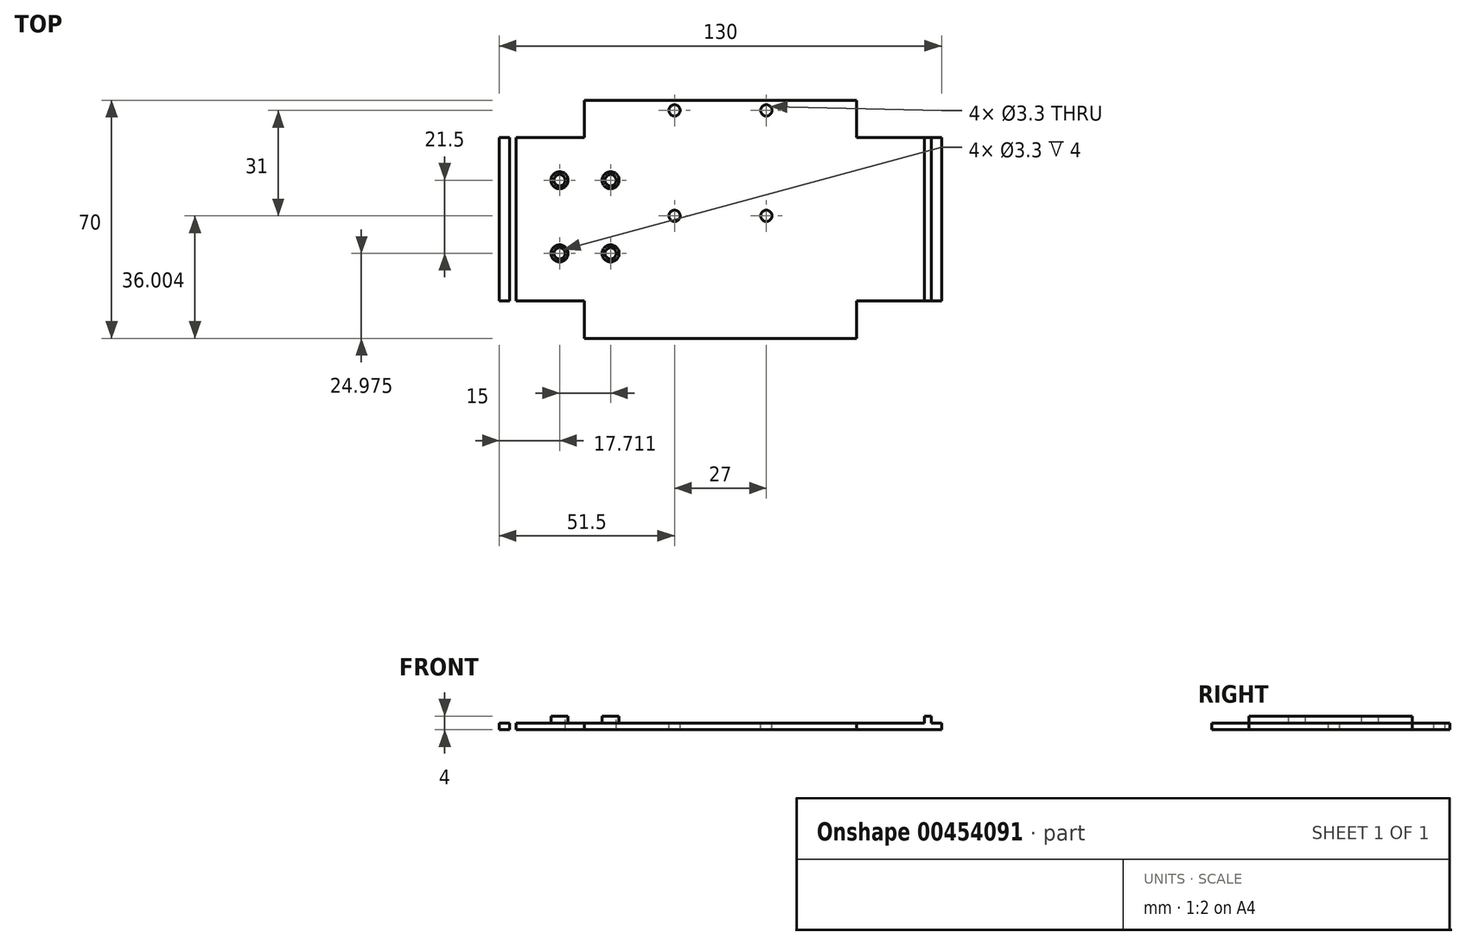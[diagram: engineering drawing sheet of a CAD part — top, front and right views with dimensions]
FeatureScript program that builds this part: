
annotation { "Feature Type Name" : "Feature", "Feature Type Description" : "" }
export const myFeature = defineFeature(function(context is Context, id is Id, definition is map)
    precondition{}
    {
        {
            var Q0;
            Q0=qCreatedBy(makeId("Top.planeOp"),FACE);
            var sketch = newSketch(context, id + "F0", { "sketchPlane" : qUnion([Q0])});
            skLineSegment(sketch, "E0.bottom", {"start": v(-50.01, 37.07) * mm, "end": v(29.99, 37.07) * mm});
            skLineSegment(sketch, "E0.top", {"start": v(-50.01, -32.93) * mm, "end": v(29.99, -32.93) * mm});
            skLineSegment(sketch, "E0.left", {"start": v(-50.01, 37.07) * mm, "end": v(-50.01, -32.93) * mm});
            skLineSegment(sketch, "E0.right", {"start": v(29.99, 37.07) * mm, "end": v(29.99, -32.93) * mm});
            skLineSegment(sketch, "E1.bottom", {"start": v(-75.01, 26.07) * mm, "end": v(54.99, 26.07) * mm});
            skLineSegment(sketch, "E1.top", {"start": v(-75.01, -21.93) * mm, "end": v(54.99, -21.93) * mm});
            skLineSegment(sketch, "E1.left", {"start": v(-75.01, 26.07) * mm, "end": v(-75.01, -21.93) * mm});
            skLineSegment(sketch, "E1.right", {"start": v(54.99, 26.07) * mm, "end": v(54.99, -21.93) * mm});
            skLineSegment(sketch, "E2.bottom", {"start": v(-72.01, 26.07) * mm, "end": v(-70.01, 26.07) * mm});
            skLineSegment(sketch, "E2.top", {"start": v(-72.01, -21.93) * mm, "end": v(-70.01, -21.93) * mm});
            skLineSegment(sketch, "E2.left", {"start": v(-72.01, 26.07) * mm, "end": v(-72.01, -21.93) * mm});
            skLineSegment(sketch, "E2.right", {"start": v(-70.01, 26.07) * mm, "end": v(-70.01, -21.93) * mm});
            skLineSegment(sketch, "E3.bottom", {"start": v(49.99, 26.07) * mm, "end": v(51.99, 26.07) * mm});
            skLineSegment(sketch, "E3.top", {"start": v(49.99, -21.93) * mm, "end": v(51.99, -21.93) * mm});
            skLineSegment(sketch, "E3.left", {"start": v(49.99, 26.07) * mm, "end": v(49.99, -21.93) * mm});
            skLineSegment(sketch, "E3.right", {"start": v(51.99, 26.07) * mm, "end": v(51.99, -21.93) * mm});
            skLineSegment(sketch, "E4.bottom", {"start": v(-23.51, 34.07) * mm, "end": v(3.49, 34.07) * mm, "construction": true});
            skLineSegment(sketch, "E4.top", {"start": v(-23.51, 3.07) * mm, "end": v(3.49, 3.07) * mm, "construction": true});
            skLineSegment(sketch, "E4.left", {"start": v(-23.51, 34.07) * mm, "end": v(-23.51, 3.07) * mm, "construction": true});
            skLineSegment(sketch, "E4.right", {"start": v(3.49, 34.07) * mm, "end": v(3.49, 3.07) * mm, "construction": true});
            skLineSegment(sketch, "E5.bottom", {"start": v(-54.29, 26.07) * mm, "end": v(-17.79, 26.07) * mm});
            skLineSegment(sketch, "E5.top", {"start": v(-54.29, -21.93) * mm, "end": v(-17.79, -21.93) * mm});
            skLineSegment(sketch, "E6.bottom", {"start": v(19.21, 26.07) * mm, "end": v(55.71, 26.07) * mm});
            skLineSegment(sketch, "E6.top", {"start": v(19.21, -21.93) * mm, "end": v(55.71, -21.93) * mm});
            skLineSegment(sketch, "E7.bottom", {"start": v(-57.3, 13.54) * mm, "end": v(-42.3, 13.54) * mm, "construction": true});
            skLineSegment(sketch, "E7.top", {"start": v(-57.3, -7.96) * mm, "end": v(-42.3, -7.96) * mm, "construction": true});
            skLineSegment(sketch, "E7.left", {"start": v(-57.3, 13.54) * mm, "end": v(-57.3, -7.96) * mm, "construction": true});
            skLineSegment(sketch, "E7.right", {"start": v(-42.3, 13.54) * mm, "end": v(-42.3, -7.96) * mm, "construction": true});
            skCircle(sketch, "E8", {"center": v(-57.3, 13.54) * mm, "radius": 2.5 * mm});
            skCircle(sketch, "E9", {"center": v(-42.3, 13.54) * mm, "radius": 2.5 * mm});
            skCircle(sketch, "E10", {"center": v(-42.3, -7.96) * mm, "radius": 2.5 * mm});
            skCircle(sketch, "E11", {"center": v(-57.3, -7.96) * mm, "radius": 2.5 * mm});
            skSolve(sketch);
        }
        {
            var Q0;
            {var subQ0=sQuery(id+"F0.wireOp",EDGE,"E1.bottom");var subQ1=sQuery(id+"F0.wireOp",EDGE,"E0.left");var subQ2=makeQuery(id+"F0.imprint","INTERSECT",VERTEX,{"derivedFrom":[subQ1,subQ0]});Q0=makeQuery(id+"F0.imprint","IMPRINT",FACE,{"disambiguationData":[TD([[makeQuery(id+"F0.imprint","IMPRINT",EDGE,{"disambiguationData":[TD([[subQ2,-1.0]])],"derivedFrom":subQ1}),1.0]])]});}
            var Q1;
            {var subQ0=sQuery(id+"F0.wireOp",EDGE,"E0.bottom");Q1=makeQuery(id+"F0.imprint","IMPRINT",FACE,{"disambiguationData":[TD([[makeQuery(id+"F0.imprint","IMPRINT",EDGE,{"derivedFrom":subQ0}),-1.0]])]});}
            var Q2;
            {var subQ5=sQuery(id+"F0.wireOp",EDGE,"E1.left");Q2=makeQuery(id+"F0.imprint","IMPRINT",FACE,{"disambiguationData":[TD([[makeQuery(id+"F0.imprint","IMPRINT",EDGE,{"derivedFrom":subQ5}),1.0]])]});}
            var Q3;
            {var subQ0=sQuery(id+"F0.wireOp",EDGE,"E0.top");Q3=makeQuery(id+"F0.imprint","IMPRINT",FACE,{"disambiguationData":[TD([[makeQuery(id+"F0.imprint","IMPRINT",EDGE,{"derivedFrom":subQ0}),1.0]])]});}
            var Q4;
            {var subQ5=sQuery(id+"F0.wireOp",EDGE,"E1.right");Q4=makeQuery(id+"F0.imprint","IMPRINT",FACE,{"disambiguationData":[TD([[makeQuery(id+"F0.imprint","IMPRINT",EDGE,{"derivedFrom":subQ5}),-1.0]])]});}
            var Q5;
            {var subQ5=sQuery(id+"F0.wireOp",EDGE,"E2.right");Q5=makeQuery(id+"F0.imprint","IMPRINT",FACE,{"disambiguationData":[TD([[makeQuery(id+"F0.imprint","IMPRINT",EDGE,{"derivedFrom":subQ5}),1.0]])]});}
            var Q6;
            Q6=makeQuery(id+"F0.imprint","IMPRINT",FACE,{"disambiguationData":[TD([[makeQuery(id+"F0.imprint","IMPRINT",EDGE,{"derivedFrom":sQuery(id+"F0.wireOp",EDGE,"E2.bottom")}),-1.0]])]});
            var Q7;
            {var subQ5=sQuery(id+"F0.wireOp",EDGE,"E3.left");Q7=makeQuery(id+"F0.imprint","IMPRINT",FACE,{"disambiguationData":[TD([[makeQuery(id+"F0.imprint","IMPRINT",EDGE,{"derivedFrom":subQ5}),-1.0]])]});}
            var Q8;
            Q8=makeQuery(id+"F0.imprint","IMPRINT",FACE,{"disambiguationData":[TD([[makeQuery(id+"F0.imprint","IMPRINT",EDGE,{"derivedFrom":sQuery(id+"F0.wireOp",EDGE,"E3.bottom")}),-1.0]])]});
            var Q9;
            {var subQ0=sQuery(id+"F0.wireOp",EDGE,"E5.right");Q9=makeQuery(id+"F0.imprint","IMPRINT",FACE,{"disambiguationData":[TD([[makeQuery(id+"F0.imprint","IMPRINT",EDGE,{"derivedFrom":subQ0}),1.0]])]});}
            var Q10;
            {var subQ5=sQuery(id+"F0.wireOp",EDGE,"E6.right");Q10=makeQuery(id+"F0.imprint","IMPRINT",FACE,{"disambiguationData":[TD([[makeQuery(id+"F0.imprint","IMPRINT",EDGE,{"derivedFrom":subQ5}),1.0]])]});}
            var Q11;
            Q11=makeQuery(id+"F0.imprint","IMPRINT",FACE,{"disambiguationData":[TD([[makeQuery(id+"F0.imprint","IMPRINT",EDGE,{"derivedFrom":sQuery(id+"F0.wireOp",EDGE,"E9")}),1.0]])]});
            var Q12;
            Q12=makeQuery(id+"F0.imprint","IMPRINT",FACE,{"disambiguationData":[TD([[makeQuery(id+"F0.imprint","IMPRINT",EDGE,{"derivedFrom":sQuery(id+"F0.wireOp",EDGE,"E10")}),1.0]])]});
            var Q13;
            Q13=makeQuery(id+"F0.imprint","IMPRINT",FACE,{"disambiguationData":[TD([[makeQuery(id+"F0.imprint","IMPRINT",EDGE,{"derivedFrom":sQuery(id+"F0.wireOp",EDGE,"E11")}),1.0]])]});
            var Q14;
            Q14=makeQuery(id+"F0.imprint","IMPRINT",FACE,{"disambiguationData":[TD([[makeQuery(id+"F0.imprint","IMPRINT",EDGE,{"derivedFrom":sQuery(id+"F0.wireOp",EDGE,"E8")}),1.0]])]});
            var Q15;
            Q15=makeQuery(id+"F0.imprint","IMPRINT",FACE,{"disambiguationData":[TD([[makeQuery(id+"F0.imprint","IMPRINT",EDGE,{"derivedFrom":sQuery(id+"F0.wireOp",EDGE,"E9")}),-1.0]])]});
            var Q16;
            {var subQ0=sQuery(id+"F0.wireOp",EDGE,"E3.left");Q16=makeQuery(id+"F0.imprint","IMPRINT",FACE,{"disambiguationData":[TD([[makeQuery(id+"F0.imprint","IMPRINT",EDGE,{"derivedFrom":subQ0}),1.0]])]});}
            extrude(context, id + "F1", {"entities" : qUnion([Q0, Q1, Q2, Q3, Q4, Q5, Q6, Q7, Q8, Q9, Q10, Q11, Q12, Q13, Q14, Q15, Q16]), "oppositeDirection" : true, "depth" : 2 * mm});
        }
        {
            var Q0;
            Q0=makeQuery(id+"F0.imprint","IMPRINT",FACE,{"disambiguationData":[TD([[makeQuery(id+"F0.imprint","IMPRINT",EDGE,{"derivedFrom":sQuery(id+"F0.wireOp",EDGE,"E2.bottom")}),-1.0]])]});
            var Q1;
            Q1=makeQuery(id+"F0.imprint","IMPRINT",FACE,{"disambiguationData":[TD([[makeQuery(id+"F0.imprint","IMPRINT",EDGE,{"derivedFrom":sQuery(id+"F0.wireOp",EDGE,"E3.bottom")}),-1.0]])]});
            var Q2;
            Q2=makeQuery(id+"F0.imprint","IMPRINT",FACE,{"disambiguationData":[TD([[makeQuery(id+"F0.imprint","IMPRINT",EDGE,{"derivedFrom":sQuery(id+"F0.wireOp",EDGE,"E8")}),1.0]])]});
            var Q3;
            Q3=makeQuery(id+"F0.imprint","IMPRINT",FACE,{"disambiguationData":[TD([[makeQuery(id+"F0.imprint","IMPRINT",EDGE,{"derivedFrom":sQuery(id+"F0.wireOp",EDGE,"E9")}),1.0]])]});
            var Q4;
            Q4=makeQuery(id+"F0.imprint","IMPRINT",FACE,{"disambiguationData":[TD([[makeQuery(id+"F0.imprint","IMPRINT",EDGE,{"derivedFrom":sQuery(id+"F0.wireOp",EDGE,"E10")}),1.0]])]});
            var Q5;
            Q5=makeQuery(id+"F0.imprint","IMPRINT",FACE,{"disambiguationData":[TD([[makeQuery(id+"F0.imprint","IMPRINT",EDGE,{"derivedFrom":sQuery(id+"F0.wireOp",EDGE,"E11")}),1.0]])]});
            var Q6;
            {var subQ0=sQuery(id+"F0.wireOp",EDGE,"E3.left");Q6=makeQuery(id+"F0.imprint","IMPRINT",FACE,{"disambiguationData":[TD([[makeQuery(id+"F0.imprint","IMPRINT",EDGE,{"derivedFrom":subQ0}),1.0]])]});}
            extrude(context, id + "F2", {"entities" : qUnion([Q0, Q1, Q2, Q3, Q4, Q5, Q6]), "operationType" : NewBodyOperationType.ADD, "depth" : 2 * mm});
        }
        {
            var Q0;
            Q0=sQuery(id+"F0.wireOp",VERTEX,"E4.top.start");
            var Q1;
            Q1=sQuery(id+"F0.wireOp",VERTEX,"E4.right.end");
            var Q2;
            Q2=sQuery(id+"F0.wireOp",VERTEX,"E4.right.start");
            var Q3;
            Q3=sQuery(id+"F0.wireOp",VERTEX,"E4.bottom.start");
            var Q4;
            Q4=sQuery(id+"F0.wireOp",VERTEX,"E8.center");
            var Q5;
            Q5=sQuery(id+"F0.wireOp",VERTEX,"E9.center");
            var Q6;
            Q6=sQuery(id+"F0.wireOp",VERTEX,"E7.right.end");
            var Q7;
            Q7=sQuery(id+"F0.wireOp",VERTEX,"E7.top.start");
            var Q8;
            Q8=makeQuery(id+"F1.opExtrude","SWEPT_BODY",BODY,{"disambiguationData":[OSD([sQuery(id+"F0.wireOp",EDGE,"E0.bottom"),sQuery(id+"F0.wireOp",EDGE,"E0.top"),sQuery(id+"F0.wireOp",EDGE,"E0.left"),sQuery(id+"F0.wireOp",EDGE,"E0.right"),sQuery(id+"F0.wireOp",EDGE,"E1.bottom"),sQuery(id+"F0.wireOp",EDGE,"E1.top"),sQuery(id+"F0.wireOp",EDGE,"E1.left"),sQuery(id+"F0.wireOp",EDGE,"E1.right"),sQuery(id+"F0.wireOp",EDGE,"E3.bottom"),sQuery(id+"F0.wireOp",EDGE,"E3.top")])]});
            hole(context, id + "F3", {"style" : HoleStyle.SIMPLE, "endStyle" : HoleEndStyle.THROUGH, "standardTappedOrClearance" : lookupTablePath({ "standard" : "ISO", "fit" : "Normal", "size" : "M3", "type" : "Clearance" }), "standardBlindInLast" : lookupTablePath({ "fit" : "Standard", "standard" : "ISO", "size" : "M3", "type" : "Clearance" }), "holeDiameter" : 3.3 * mm, "isTappedThrough" : true, "tappedDepth" : 12 * mm, "tapClearance" : 3, "locations" : qUnion([Q0, Q1, Q2, Q3, Q4, Q5, Q6, Q7]), "scope" : qUnion([Q8])});
        }
        {
            var Q0;
            Q0=sQuery(id+"F0.wireOp",VERTEX,"E8.center");
            var Q1;
            Q1=sQuery(id+"F0.wireOp",VERTEX,"E7.top.start");
            var Q2;
            Q2=sQuery(id+"F0.wireOp",VERTEX,"E9.center");
            var Q3;
            Q3=sQuery(id+"F0.wireOp",VERTEX,"E7.right.end");
            var Q4;
            Q4=makeQuery(id+"F1.opExtrude","SWEPT_BODY",BODY,{"disambiguationData":[OSD([sQuery(id+"F0.wireOp",EDGE,"E0.bottom"),sQuery(id+"F0.wireOp",EDGE,"E0.top"),sQuery(id+"F0.wireOp",EDGE,"E0.left"),sQuery(id+"F0.wireOp",EDGE,"E0.right"),sQuery(id+"F0.wireOp",EDGE,"E1.bottom"),sQuery(id+"F0.wireOp",EDGE,"E1.top"),sQuery(id+"F0.wireOp",EDGE,"E1.left"),sQuery(id+"F0.wireOp",EDGE,"E1.right"),sQuery(id+"F0.wireOp",EDGE,"E2.bottom"),sQuery(id+"F0.wireOp",EDGE,"E2.top"),sQuery(id+"F0.wireOp",EDGE,"E3.bottom"),sQuery(id+"F0.wireOp",EDGE,"E3.top")])]});
            hole(context, id + "F4", {"style" : HoleStyle.SIMPLE, "endStyle" : HoleEndStyle.THROUGH, "oppositeDirection" : true, "standardTappedOrClearance" : lookupTablePath({ "standard" : "ISO", "fit" : "Normal", "size" : "M3", "type" : "Clearance" }), "standardBlindInLast" : lookupTablePath({ "fit" : "Standard", "standard" : "ISO", "size" : "M3", "type" : "Clearance" }), "holeDiameter" : 3.3 * mm, "isTappedThrough" : true, "tappedDepth" : 12 * mm, "tapClearance" : 3, "locations" : qUnion([Q0, Q1, Q2, Q3]), "scope" : qUnion([Q4])});
        }
    });
